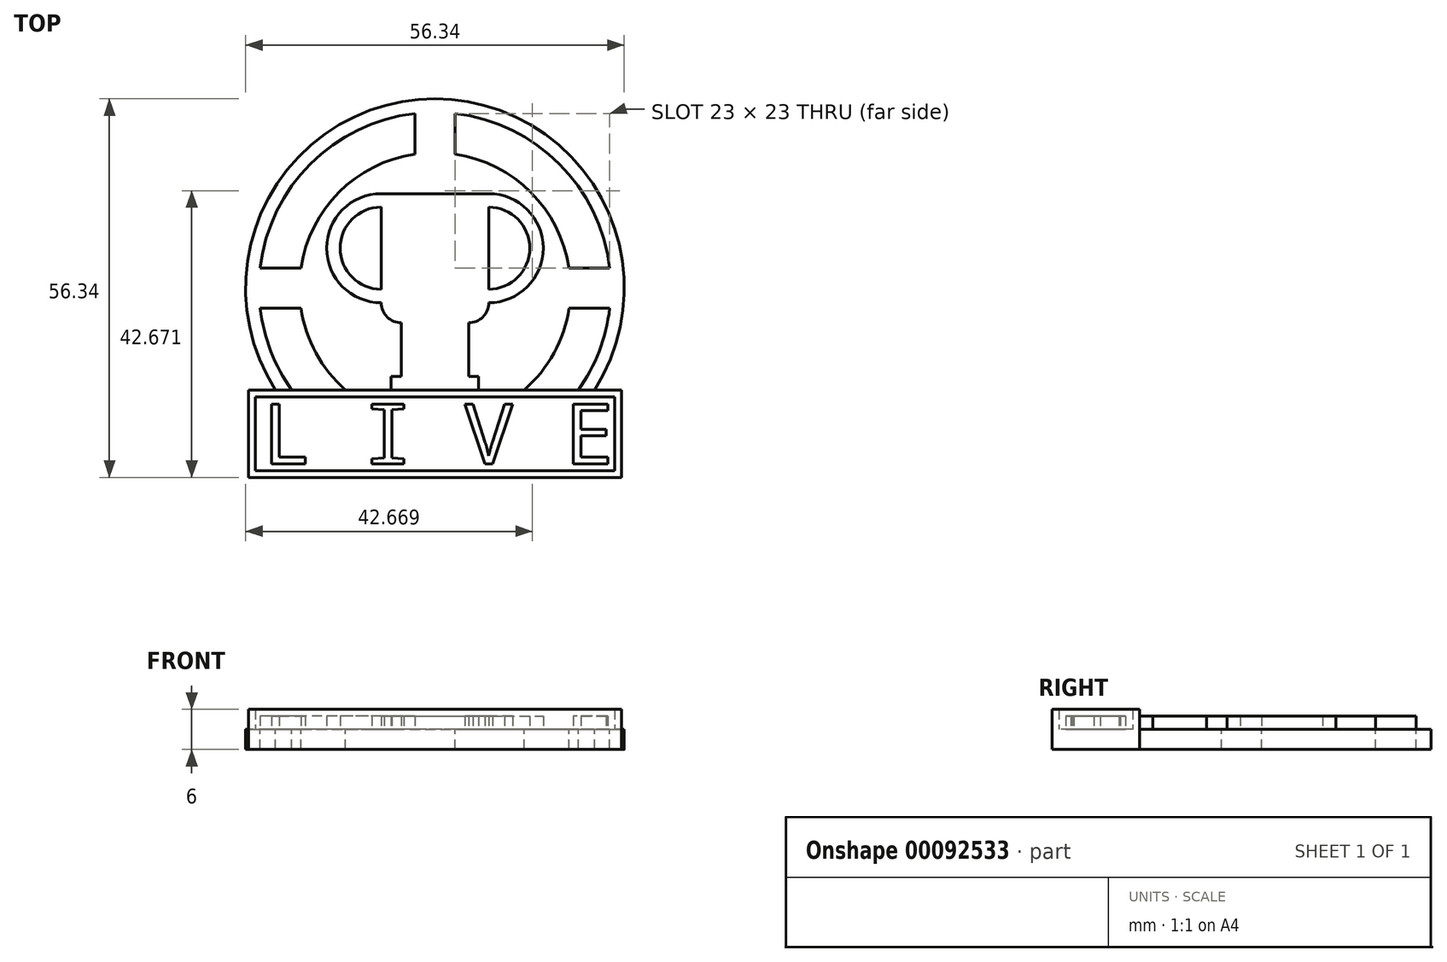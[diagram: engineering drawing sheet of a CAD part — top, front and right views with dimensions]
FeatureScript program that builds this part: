
annotation { "Feature Type Name" : "Feature", "Feature Type Description" : "" }
export const myFeature = defineFeature(function(context is Context, id is Id, definition is map)
    precondition{}
    {
        {
            var Q0;
            Q0=qCreatedBy(makeId("Top.planeOp"),FACE);
            var sketch = newSketch(context, id + "F0", { "sketchPlane" : qUnion([Q0])});
            skText(sketch, "E0", { "text": "L I V E", "fontName": "DroidSansMono.ttf"});
            const initialGuessF0  = {"E0": [-0.02574, 0, 1, 0, 0.009]};
            skSetInitialGuess(sketch, initialGuessF0);
            skSolve(sketch);
        }
        {
            var Q0;
            Q0=qCreatedBy(makeId("Top.planeOp"),FACE);
            var sketch = newSketch(context, id + "F1", { "sketchPlane" : qUnion([Q0])});
            skLineSegment(sketch, "E1", {"start": v(-27.74, -2) * mm, "end": v(27.74, -2) * mm});
            skLineSegment(sketch, "E2", {"start": v(27.74, -2) * mm, "end": v(27.74, 11) * mm});
            skLineSegment(sketch, "E3", {"start": v(27.74, 11) * mm, "end": v(-27.74, 11) * mm});
            skLineSegment(sketch, "E4", {"start": v(-27.74, 11) * mm, "end": v(-27.74, -2) * mm});
            skSolve(sketch);
        }
        {
            var Q0;
            Q0=qSketchRegion(id+"F1",true);
            extrude(context, id + "F2", {"entities" : qUnion([Q0]), "oppositeDirection" : true, "depth" : 3 * mm});
        }
        {
            var Q0;
            Q0=qCreatedBy(makeId("Top.planeOp"),FACE);
            var sketch = newSketch(context, id + "F3", { "sketchPlane" : qUnion([Q0])});
            skPoint(sketch, "E5", {"position": v(-23.74, 11) * mm});
            skPoint(sketch, "E6", {"position": v(23.74, 11) * mm});
            skArc(sketch, "E7", {"start": v(23.74, 11) * mm, "mid": v(0, 54.34) * mm, "end": v(-23.74, 11) * mm});
            skPoint(sketch, "E7.third.point", {"position": v(0, 54.34) * mm});
            skLineSegment(sketch, "E8", {"start": v(0, 26.17) * mm, "end": v(0, 54.34) * mm, "construction": true});
            skArc(sketch, "E9", {"start": v(21.33, 11) * mm, "mid": v(24.43, 16.8) * mm, "end": v(26, 23.17) * mm});
            skLineSegment(sketch, "E10", {"start": v(-28.17, 26.17) * mm, "end": v(0, 26.17) * mm, "construction": true});
            skArc(sketch, "E11", {"start": v(13.3, 11) * mm, "mid": v(17.7, 16.5) * mm, "end": v(19.95, 23.17) * mm});
            skLineSegment(sketch, "E12", {"start": v(-23.74, 11) * mm, "end": v(23.74, 11) * mm});
            skLineSegment(sketch, "E13.trimOffspring", {"start": v(-3, 46.12) * mm, "end": v(-3, 52.17) * mm});
            skLineSegment(sketch, "E14.trimOffspring", {"start": v(3, 46.12) * mm, "end": v(3, 52.17) * mm});
            skLineSegment(sketch, "E15.trimOffspring", {"start": v(-19.95, 29.17) * mm, "end": v(-26, 29.17) * mm});
            skLineSegment(sketch, "E16.trimOffspring", {"start": v(-19.95, 23.17) * mm, "end": v(-26, 23.17) * mm});
            skArc(sketch, "E17.trimOffspring", {"start": v(-19.95, 23.17) * mm, "mid": v(-17.7, 16.5) * mm, "end": v(-13.3, 11) * mm});
            skArc(sketch, "E18.trimOffspring", {"start": v(-26, 23.17) * mm, "mid": v(-24.43, 16.8) * mm, "end": v(-21.33, 11) * mm});
            skArc(sketch, "E19.trimOffspring", {"start": v(-3, 46.12) * mm, "mid": v(-14.26, 40.43) * mm, "end": v(-19.95, 29.17) * mm});
            skArc(sketch, "E20.trimOffspring", {"start": v(-3, 52.17) * mm, "mid": v(-18.5, 44.68) * mm, "end": v(-26, 29.17) * mm});
            skLineSegment(sketch, "E21.trimOffspring", {"start": v(19.95, 29.17) * mm, "end": v(26, 29.17) * mm});
            skLineSegment(sketch, "E22.trimOffspring", {"start": v(19.95, 23.17) * mm, "end": v(26, 23.17) * mm});
            skArc(sketch, "E23.trimOffspring", {"start": v(19.95, 29.17) * mm, "mid": v(14.26, 40.43) * mm, "end": v(3, 46.12) * mm});
            skArc(sketch, "E24.trimOffspring", {"start": v(26, 29.17) * mm, "mid": v(18.5, 44.68) * mm, "end": v(3, 52.17) * mm});
            skSolve(sketch);
        }
        {
            var Q0;
            {var subQ1=sQuery(id+"F3.wireOp",EDGE,"E7");Q0=makeQuery(id+"F3.imprint","IMPRINT",FACE,{"disambiguationData":[TD([[makeQuery(id+"F3.imprint","IMPRINT",EDGE,{"derivedFrom":subQ1}),1.0]])]});}
            var Q1;
            Q1=makeQuery(id+"F2.opExtrude","CAP_FACE",FACE,{"disambiguationData":[OSD([sQuery(id+"F1.wireOp",EDGE,"E1"),sQuery(id+"F1.wireOp",EDGE,"E2"),sQuery(id+"F1.wireOp",EDGE,"E3"),sQuery(id+"F1.wireOp",EDGE,"E4")])],"isStart":false});
            extrude(context, id + "F4", {"entities" : qUnion([Q0]), "operationType" : NewBodyOperationType.ADD, "oppositeDirection" : true, "endBoundEntityFace" : qUnion([Q1]), "depth" : 3 * mm});
        }
        {
            var Q0;
            Q0=makeQuery(id+"F4.boolean.opBoolean","MERGE",FACE,{"derivedFrom":[makeQuery(id+"F2.opExtrude","CAP_FACE",FACE,{"disambiguationData":[OSD([sQuery(id+"F1.wireOp",EDGE,"E1"),sQuery(id+"F1.wireOp",EDGE,"E2"),sQuery(id+"F1.wireOp",EDGE,"E3"),sQuery(id+"F1.wireOp",EDGE,"E4")])],"isStart":true}),makeQuery(id+"F4.opExtrude","CAP_FACE",FACE,{"disambiguationData":[OSD([sQuery(id+"F3.wireOp",EDGE,"E7"),sQuery(id+"F3.wireOp",EDGE,"E9"),sQuery(id+"F3.wireOp",EDGE,"E11"),sQuery(id+"F3.wireOp",EDGE,"E12"),sQuery(id+"F3.wireOp",EDGE,"E13.trimOffspring"),sQuery(id+"F3.wireOp",EDGE,"E14.trimOffspring"),sQuery(id+"F3.wireOp",EDGE,"E15.trimOffspring"),sQuery(id+"F3.wireOp",EDGE,"E16.trimOffspring"),sQuery(id+"F3.wireOp",EDGE,"E17.trimOffspring"),sQuery(id+"F3.wireOp",EDGE,"E18.trimOffspring"),sQuery(id+"F3.wireOp",EDGE,"E19.trimOffspring"),sQuery(id+"F3.wireOp",EDGE,"E20.trimOffspring"),sQuery(id+"F3.wireOp",EDGE,"E21.trimOffspring"),sQuery(id+"F3.wireOp",EDGE,"E22.trimOffspring"),sQuery(id+"F3.wireOp",EDGE,"E23.trimOffspring"),sQuery(id+"F3.wireOp",EDGE,"E24.trimOffspring")])],"isStart":true})]});
            var sketch = newSketch(context, id + "F5", { "sketchPlane" : qUnion([Q0])});
            skLineSegment(sketch, "E25", {"start": v(-10, 40.23) * mm, "end": v(8, 40.23) * mm});
            skLineSegment(sketch, "E26", {"start": v(0, 0) * mm, "end": v(0, 54.34) * mm, "construction": true});
            skLineSegment(sketch, "E27", {"start": v(-13.3, 11) * mm, "end": v(13.3, 11) * mm, "construction": true});
            skLineSegment(sketch, "E28", {"start": v(-6.5, 11) * mm, "end": v(6.5, 11) * mm});
            skPoint(sketch, "E29", {"position": v(0, 11) * mm});
            skLineSegment(sketch, "E30", {"start": v(6.5, 11) * mm, "end": v(6.5, 13) * mm});
            skLineSegment(sketch, "E31", {"start": v(6.5, 13) * mm, "end": v(5, 13) * mm});
            skLineSegment(sketch, "E32", {"start": v(5, 13) * mm, "end": v(5, 21) * mm});
            skLineSegment(sketch, "E33", {"start": v(5, 21) * mm, "end": v(5, 21) * mm});
            skLineSegment(sketch, "E34", {"start": v(8, 26) * mm, "end": v(8, 38.23) * mm});
            skPoint(sketch, "E35.visualSharp", {"position": v(8, 21) * mm});
            skArc(sketch, "E35.filletArc", {"start": v(5, 21) * mm, "mid": v(7.12, 21.88) * mm, "end": v(8, 24) * mm});
            skArc(sketch, "E36", {"start": v(8, 24) * mm, "mid": v(16.11, 32.11) * mm, "end": v(8, 40.23) * mm});
            skArc(sketch, "E37", {"start": v(8, 26) * mm, "mid": v(14.11, 32.11) * mm, "end": v(8, 38.23) * mm});
            skArc(sketch, "E38.MirrorCS", {"start": v(-8, 24) * mm, "mid": v(-16.11, 32.11) * mm, "end": v(-8, 40.23) * mm});
            skArc(sketch, "E39.MirrorCS", {"start": v(-8, 26) * mm, "mid": v(-14.11, 32.11) * mm, "end": v(-8, 38.23) * mm});
            skLineSegment(sketch, "E40.MirrorCS", {"start": v(-8, 26) * mm, "end": v(-8, 38.23) * mm});
            skArc(sketch, "E41.MirrorCS", {"start": v(-5, 21) * mm, "mid": v(-7.12, 21.88) * mm, "end": v(-8, 24) * mm});
            skLineSegment(sketch, "E42.MirrorCS", {"start": v(-5, 21) * mm, "end": v(-5, 21) * mm});
            skLineSegment(sketch, "E43.MirrorCS", {"start": v(-5, 13) * mm, "end": v(-5, 21) * mm});
            skLineSegment(sketch, "E44.MirrorCS", {"start": v(-6.5, 13) * mm, "end": v(-5, 13) * mm});
            skLineSegment(sketch, "E45.MirrorCS", {"start": v(-6.5, 11) * mm, "end": v(-6.5, 13) * mm});
            skSolve(sketch);
        }
        {
            var Q0;
            Q0=qSketchRegion(id+"F5",true);
            extrude(context, id + "F6", {"entities" : qUnion([Q0]), "operationType" : NewBodyOperationType.ADD, "depth" : 2 * mm, "hasSecondDirection" : true, "secondDirectionOppositeDirection" : true, "secondDirectionDepth" : 2 * mm});
        }
        {
            var Q0;
            Q0=makeQuery(id+"F4.boolean.opBoolean","MERGE",FACE,{"derivedFrom":[makeQuery(id+"F2.opExtrude","CAP_FACE",FACE,{"disambiguationData":[OSD([sQuery(id+"F1.wireOp",EDGE,"E1"),sQuery(id+"F1.wireOp",EDGE,"E2"),sQuery(id+"F1.wireOp",EDGE,"E3"),sQuery(id+"F1.wireOp",EDGE,"E4")])],"isStart":false}),makeQuery(id+"F4.opExtrude","CAP_FACE",FACE,{"disambiguationData":[OSD([sQuery(id+"F3.wireOp",EDGE,"E7"),sQuery(id+"F3.wireOp",EDGE,"E9"),sQuery(id+"F3.wireOp",EDGE,"E11"),sQuery(id+"F3.wireOp",EDGE,"E12"),sQuery(id+"F3.wireOp",EDGE,"E13.trimOffspring"),sQuery(id+"F3.wireOp",EDGE,"E14.trimOffspring"),sQuery(id+"F3.wireOp",EDGE,"E15.trimOffspring"),sQuery(id+"F3.wireOp",EDGE,"E16.trimOffspring"),sQuery(id+"F3.wireOp",EDGE,"E17.trimOffspring"),sQuery(id+"F3.wireOp",EDGE,"E18.trimOffspring"),sQuery(id+"F3.wireOp",EDGE,"E19.trimOffspring"),sQuery(id+"F3.wireOp",EDGE,"E20.trimOffspring"),sQuery(id+"F3.wireOp",EDGE,"E21.trimOffspring"),sQuery(id+"F3.wireOp",EDGE,"E22.trimOffspring"),sQuery(id+"F3.wireOp",EDGE,"E23.trimOffspring"),sQuery(id+"F3.wireOp",EDGE,"E24.trimOffspring")])],"isStart":false})]});
            var sketch = newSketch(context, id + "F7", { "sketchPlane" : qUnion([Q0])});
            skArc(sketch, "E46", {"start": v(-26, -29.17) * mm, "mid": v(-18.5, -44.68) * mm, "end": v(-3, -52.17) * mm});
            skArc(sketch, "E47", {"start": v(-19.95, -29.17) * mm, "mid": v(-14.26, -40.43) * mm, "end": v(-3, -46.12) * mm});
            skLineSegment(sketch, "E48", {"start": v(-3, -52.17) * mm, "end": v(-3, -46.12) * mm});
            skLineSegment(sketch, "E49", {"start": v(-19.95, -29.17) * mm, "end": v(-26, -29.17) * mm});
            skSolve(sketch);
        }
        {
            var Q0;
            Q0=qSketchRegion(id+"F7",true);
            extrude(context, id + "F8", {"entities" : qUnion([Q0]), "operationType" : NewBodyOperationType.ADD, "oppositeDirection" : true, "depth" : 5 * mm});
        }
        {
            var Q0;
            Q0 = qSketchRegion(id + "F0", true);
            extrude(context, id + "F9", {"entities" : qUnion([Q0]), "operationType" : NewBodyOperationType.ADD, "depth" : 2 * mm});
        }
        {
            var Q0;
            {var subQ0=sQuery(id+"F3.wireOp",EDGE,"E24.trimOffspring");var subQ1=sQuery(id+"F3.wireOp",EDGE,"E23.trimOffspring");var subQ2=sQuery(id+"F3.wireOp",EDGE,"E22.trimOffspring");var subQ3=sQuery(id+"F3.wireOp",EDGE,"E21.trimOffspring");var subQ4=sQuery(id+"F3.wireOp",EDGE,"E20.trimOffspring");var subQ5=sQuery(id+"F3.wireOp",EDGE,"E14.trimOffspring");var subQ6=sQuery(id+"F3.wireOp",EDGE,"E19.trimOffspring");var subQ7=sQuery(id+"F3.wireOp",EDGE,"E13.trimOffspring");var subQ8=sQuery(id+"F3.wireOp",EDGE,"E18.trimOffspring");var subQ9=sQuery(id+"F1.wireOp",EDGE,"E2");var subQ10=sQuery(id+"F3.wireOp",EDGE,"E9");var subQ11=sQuery(id+"F3.wireOp",EDGE,"E17.trimOffspring");var subQ12=sQuery(id+"F1.wireOp",EDGE,"E1");var subQ13=sQuery(id+"F3.wireOp",EDGE,"E16.trimOffspring");var subQ14=sQuery(id+"F1.wireOp",EDGE,"E3");var subQ15=sQuery(id+"F3.wireOp",EDGE,"E15.trimOffspring");var subQ16=sQuery(id+"F3.wireOp",EDGE,"E11");var subQ17=sQuery(id+"F3.wireOp",EDGE,"E7");var subQ18=sQuery(id+"F1.wireOp",EDGE,"E4");Q0=makeQuery(id+"F6.boolean.opBoolean","SPLIT",FACE,{"disambiguationData":[TD([makeQuery(id+"F2.opExtrude","SWEPT_FACE",FACE,{"disambiguationData":[OSD([subQ12])]})])],"derivedFrom":makeQuery(id+"F4.boolean.opBoolean","MERGE",FACE,{"derivedFrom":[makeQuery(id+"F2.opExtrude","CAP_FACE",FACE,{"disambiguationData":[OSD([subQ12,subQ9,subQ14,subQ18])],"isStart":true}),makeQuery(id+"F4.opExtrude","CAP_FACE",FACE,{"disambiguationData":[OSD([subQ17,subQ10,subQ16,sQuery(id+"F3.wireOp",EDGE,"E12"),subQ7,subQ5,subQ15,subQ13,subQ11,subQ8,subQ6,subQ4,subQ3,subQ2,subQ1,subQ0])],"isStart":true})]})});}
            var sketch = newSketch(context, id + "F10", { "sketchPlane" : qUnion([Q0])});
            skLineSegment(sketch, "E50.bottom", {"start": v(-27.74, 11) * mm, "end": v(27.74, 11) * mm});
            skLineSegment(sketch, "E50.top", {"start": v(-27.74, -2) * mm, "end": v(27.74, -2) * mm});
            skLineSegment(sketch, "E50.left", {"start": v(-27.74, 11) * mm, "end": v(-27.74, -2) * mm});
            skLineSegment(sketch, "E50.right", {"start": v(27.74, 11) * mm, "end": v(27.74, -2) * mm});
            skLineSegment(sketch, "E51.bottom", {"start": v(-26.74, 10) * mm, "end": v(26.74, 10) * mm});
            skLineSegment(sketch, "E51.top", {"start": v(-26.74, -1) * mm, "end": v(26.74, -1) * mm});
            skLineSegment(sketch, "E51.left", {"start": v(-26.74, 10) * mm, "end": v(-26.74, -1) * mm});
            skLineSegment(sketch, "E51.right", {"start": v(26.74, 10) * mm, "end": v(26.74, -1) * mm});
            skSolve(sketch);
        }
        {
            var Q0;
            Q0 = qSketchRegion(id + "F10", true);
            extrude(context, id + "F11", {"entities" : qUnion([Q0]), "operationType" : NewBodyOperationType.ADD, "depth" : 3 * mm});
        }
    });
